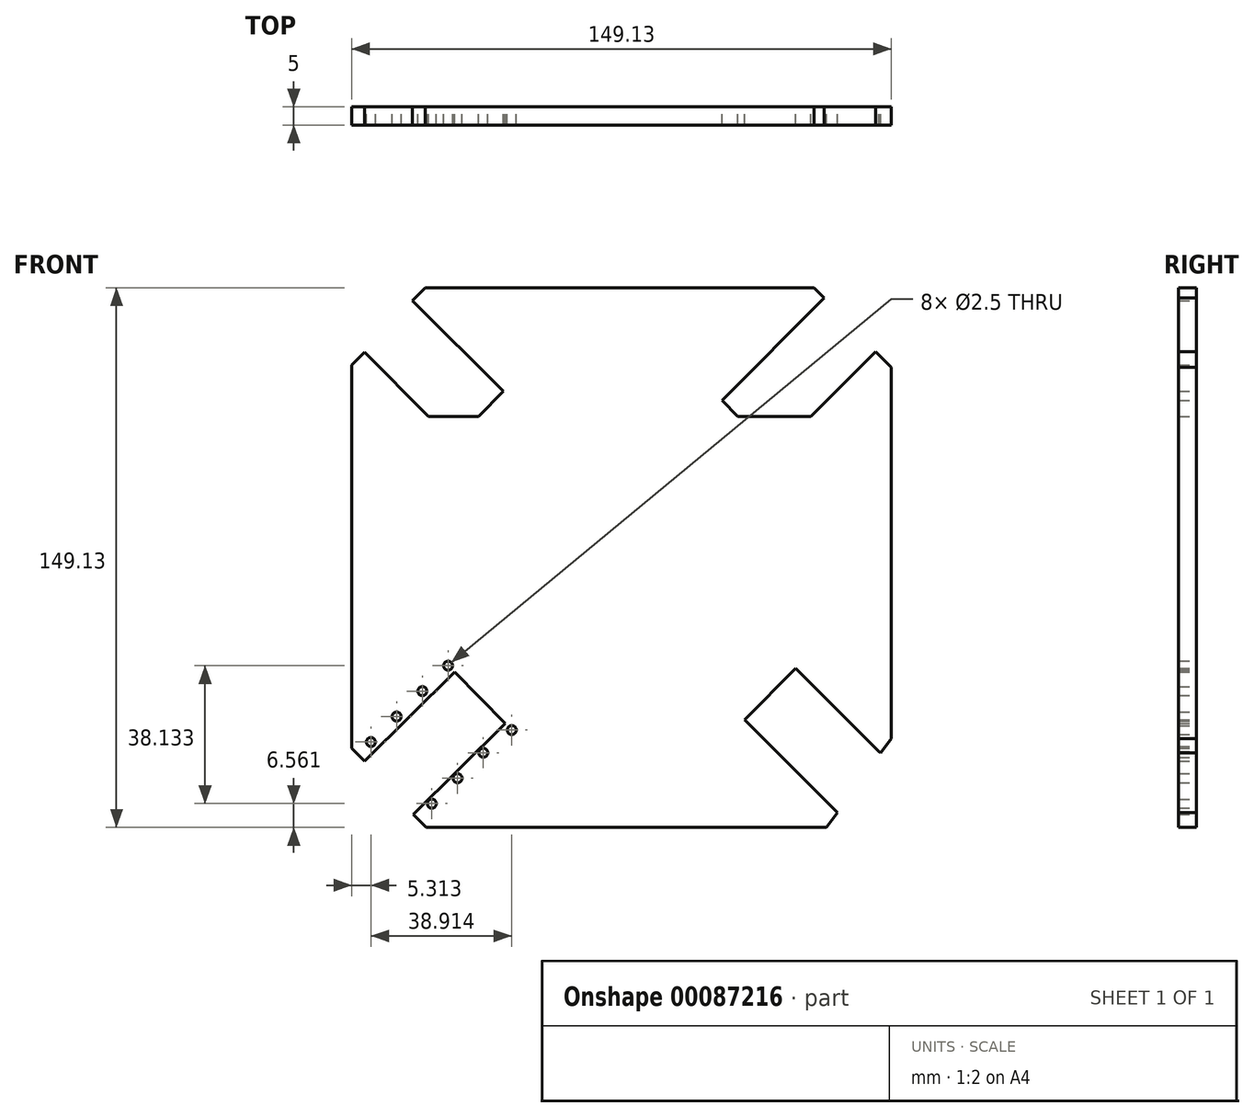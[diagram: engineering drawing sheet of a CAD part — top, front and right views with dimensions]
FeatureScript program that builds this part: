
annotation { "Feature Type Name" : "Feature", "Feature Type Description" : "" }
export const myFeature = defineFeature(function(context is Context, id is Id, definition is map)
    precondition{}
    {
        {
            var Q0;
            Q0=qCreatedBy(makeId("Front.planeOp"),FACE);
            var sketch = newSketch(context, id + "F0", { "sketchPlane" : qUnion([Q0])});
            skLineSegment(sketch, "E0.bottom", {"start": v(-47.44, 71.4) * mm, "end": v(60, 71.4) * mm});
            skLineSegment(sketch, "E0.top", {"start": v(-47.23, -77.73) * mm, "end": v(63.46, -77.73) * mm});
            skLineSegment(sketch, "E0.left", {"start": v(-67.78, 50.05) * mm, "end": v(-67.78, -55.88) * mm});
            skLineSegment(sketch, "E0.right", {"start": v(81.35, 49.41) * mm, "end": v(81.35, -3.16) * mm});
            skLineSegment(sketch, "E1", {"start": v(81.35, 71.4) * mm, "end": v(42.4, 32.45) * mm});
            skLineSegment(sketch, "E2", {"start": v(6.79, 34.12) * mm, "end": v(6.79, 71.4) * mm});
            skLineSegment(sketch, "E3.0", {"start": v(-64.24, 53.59) * mm, "end": v(-39.65, 29) * mm});
            skLineSegment(sketch, "E4.0", {"start": v(-50.97, 67.86) * mm, "end": v(-25.88, 42.77) * mm});
            skPoint(sketch, "E5.orphan", {"position": v(-30.5, -3.16) * mm});
            skPoint(sketch, "E6.orphan", {"position": v(-30.5, 34.12) * mm});
            skPoint(sketch, "E7.end.orphan", {"position": v(-30.5, 71.4) * mm});
            skPoint(sketch, "E8.orphan", {"position": v(-67.78, 71.4) * mm});
            skLineSegment(sketch, "E9.trimOffspring", {"start": v(54.92, -33.83) * mm, "end": v(77.9, -56.8) * mm});
            skLineSegment(sketch, "E10.trimOffspring", {"start": v(40.77, -47.97) * mm, "end": v(66.44, -73.64) * mm});
            skPoint(sketch, "E11.trimOffspring.end.orphan", {"position": v(81.35, -77.73) * mm});
            skLineSegment(sketch, "E12.0", {"start": v(-47.44, 71.4) * mm, "end": v(-27.61, 51.58) * mm});
            skLineSegment(sketch, "E13.0", {"start": v(-67.78, 50.05) * mm, "end": v(-44.42, 26.7) * mm});
            skLineSegment(sketch, "E14.0", {"start": v(-66, 51.82) * mm, "end": v(-44.42, 30.23) * mm});
            skLineSegment(sketch, "E15.0", {"start": v(-49.2, 69.63) * mm, "end": v(-29.38, 49.8) * mm});
            skLineSegment(sketch, "E16", {"start": v(-32.76, 35.88) * mm, "end": v(-59.78, 62.9) * mm});
            skLineSegment(sketch, "E17.0", {"start": v(62.84, 68.57) * mm, "end": v(34.56, 40.28) * mm});
            skLineSegment(sketch, "E18.0", {"start": v(77.01, 53.75) * mm, "end": v(49.05, 25.79) * mm});
            skLineSegment(sketch, "E19.0", {"start": v(60, 71.4) * mm, "end": v(31.73, 43.12) * mm});
            skLineSegment(sketch, "E20.0", {"start": v(81.35, 49.41) * mm, "end": v(53.39, 21.45) * mm});
            skLineSegment(sketch, "E21", {"start": v(31.73, 43.12) * mm, "end": v(53.39, 21.45) * mm});
            skPoint(sketch, "E22.orphan", {"position": v(6.79, 34.12) * mm});
            skPoint(sketch, "E23.orphan", {"position": v(44.07, -3.16) * mm});
            skLineSegment(sketch, "E24.0", {"start": v(28.05, 39.72) * mm, "end": v(49.26, 18.5) * mm});
            skLineSegment(sketch, "E25", {"start": v(54.92, -33.83) * mm, "end": v(40.77, -47.97) * mm});
            skLineSegment(sketch, "E26.0", {"start": v(37.24, -47.97) * mm, "end": v(64.95, -75.68) * mm});
            skLineSegment(sketch, "E27.0", {"start": v(30.17, -44.43) * mm, "end": v(63.46, -77.73) * mm});
            skLineSegment(sketch, "E28", {"start": v(54.83, -30.2) * mm, "end": v(79.67, -55.04) * mm});
            skLineSegment(sketch, "E29", {"start": v(54.83, -30.2) * mm, "end": v(37.24, -47.97) * mm});
            skLineSegment(sketch, "E30", {"start": v(51.38, -23.22) * mm, "end": v(81.35, -53.19) * mm});
            skPoint(sketch, "E31", {"position": v(68.1, -43.47) * mm});
            skLineSegment(sketch, "E32", {"start": v(46.04, -39.09) * mm, "end": v(74.17, -67.23) * mm});
            skPoint(sketch, "E33.0.start.orphan", {"position": v(-40.88, 30.23) * mm});
            skLineSegment(sketch, "E34", {"start": v(-39.65, 29) * mm, "end": v(-25.88, 42.77) * mm});
            skPoint(sketch, "E35.orphan", {"position": v(6.79, -40.45) * mm});
            skLineSegment(sketch, "E36.trimOffspring", {"start": v(-36.5, -32) * mm, "end": v(-64.26, -59.44) * mm});
            skLineSegment(sketch, "E37.trimOffspring", {"start": v(-25.32, -49.05) * mm, "end": v(-50.74, -74.17) * mm});
            skLineSegment(sketch, "E38", {"start": v(-40.03, -27.05) * mm, "end": v(-38.3, -28.8) * mm});
            skLineSegment(sketch, "E39", {"start": v(81.35, -3.16) * mm, "end": v(81.35, -53.19) * mm});
            skLineSegment(sketch, "E40", {"start": v(81.35, 49.41) * mm, "end": v(77.01, 53.75) * mm});
            skLineSegment(sketch, "E41", {"start": v(60, 71.4) * mm, "end": v(62.84, 68.57) * mm});
            skLineSegment(sketch, "E42", {"start": v(-67.78, 50.05) * mm, "end": v(-64.24, 53.59) * mm});
            skLineSegment(sketch, "E43", {"start": v(-47.44, 71.4) * mm, "end": v(-50.97, 67.86) * mm});
            skLineSegment(sketch, "E44", {"start": v(-67.78, -55.88) * mm, "end": v(-64.26, -59.44) * mm});
            skLineSegment(sketch, "E45", {"start": v(-47.23, -77.73) * mm, "end": v(-50.74, -74.17) * mm});
            skPoint(sketch, "E46.orphan", {"position": v(6.79, -3.16) * mm});
            skPoint(sketch, "E47.trimOffspring.end.orphan", {"position": v(81.35, -56.72) * mm});
            skLineSegment(sketch, "E48", {"start": v(63.46, -77.73) * mm, "end": v(66.44, -73.64) * mm});
            skLineSegment(sketch, "E49", {"start": v(77.9, -56.8) * mm, "end": v(78.43, -57.2) * mm});
            skLineSegment(sketch, "E50", {"start": v(79.67, -55.04) * mm, "end": v(79.88, -55.2) * mm});
            skPoint(sketch, "E51.start.orphan", {"position": v(67, -77.73) * mm});
            skLineSegment(sketch, "E52.trimOffspring", {"start": v(78.43, -57.2) * mm, "end": v(81.35, -53.19) * mm});
            skPoint(sketch, "E53.end.orphan", {"position": v(-67.78, -3.16) * mm});
            skPoint(sketch, "E54.end.orphan", {"position": v(6.79, -77.73) * mm});
            skLineSegment(sketch, "E55.trimOffspring", {"start": v(53.06, -60.26) * mm, "end": v(52.12, -62.85) * mm});
            skLineSegment(sketch, "E56", {"start": v(61.43, 69.98) * mm, "end": v(33.14, 41.7) * mm});
            skPoint(sketch, "E57", {"position": v(59.3, 65.03) * mm});
            skPoint(sketch, "E58", {"position": v(52.23, 57.96) * mm});
            skPoint(sketch, "E59", {"position": v(45.16, 50.9) * mm});
            skPoint(sketch, "E60", {"position": v(38.1, 43.82) * mm});
            skPoint(sketch, "E61", {"position": v(-62.47, -54.14) * mm});
            skPoint(sketch, "E62", {"position": v(-55.36, -47.1) * mm});
            skPoint(sketch, "E63", {"position": v(-48.25, -40.07) * mm});
            skPoint(sketch, "E64", {"position": v(-41.15, -33.04) * mm});
            skPoint(sketch, "E65", {"position": v(-38.33, -30.25) * mm});
            skLineSegment(sketch, "E66", {"start": v(-62.47, -54.14) * mm, "end": v(-62.46, -54.14) * mm});
            skLineSegment(sketch, "E67", {"start": v(-55.36, -47.1) * mm, "end": v(-55.35, -47.11) * mm});
            skLineSegment(sketch, "E68", {"start": v(-48.25, -40.07) * mm, "end": v(-48.24, -40.09) * mm});
            skCircle(sketch, "E69", {"center": v(-62.47, -54.14) * mm, "radius": 1.25 * mm});
            skCircle(sketch, "E70", {"center": v(-55.36, -47.1) * mm, "radius": 1.25 * mm});
            skCircle(sketch, "E71", {"center": v(-48.25, -40.07) * mm, "radius": 1.25 * mm});
            skCircle(sketch, "E72", {"center": v(-41.15, -33.04) * mm, "radius": 1.25 * mm});
            skCircle(sketch, "E73", {"center": v(-23.55, -50.84) * mm, "radius": 1.25 * mm});
            skCircle(sketch, "E74", {"center": v(-31.41, -57.11) * mm, "radius": 1.25 * mm});
            skCircle(sketch, "E75", {"center": v(-38.53, -64.14) * mm, "radius": 1.25 * mm});
            skCircle(sketch, "E76", {"center": v(-45.64, -71.17) * mm, "radius": 1.25 * mm});
            skPoint(sketch, "E77.end.orphan", {"position": v(-17.76, -47.09) * mm});
            skPoint(sketch, "E78.trimOffspring.end.orphan", {"position": v(-67.78, -77.73) * mm});
            skPoint(sketch, "E79.orphan", {"position": v(-21.27, -47.09) * mm});
            skPoint(sketch, "E80.orphan", {"position": v(-66.02, -57.66) * mm});
            skLineSegment(sketch, "E81.trimOffspring", {"start": v(-61.59, -55.03) * mm, "end": v(-60.7, -55.92) * mm});
            skLineSegment(sketch, "E82.trimOffspring", {"start": v(-54.48, -48) * mm, "end": v(-53.6, -48.9) * mm});
            skLineSegment(sketch, "E83.trimOffspring", {"start": v(-47.37, -40.96) * mm, "end": v(-46.48, -41.86) * mm});
            skLineSegment(sketch, "E84.trimOffspring", {"start": v(-39.37, -34.83) * mm, "end": v(-25.32, -49.05) * mm});
            skLineSegment(sketch, "E85", {"start": v(-32.76, 35.88) * mm, "end": v(-67.78, 35.88) * mm});
            skLineSegment(sketch, "E86", {"start": v(-32.76, 35.88) * mm, "end": v(81.35, 35.88) * mm});
            skSolve(sketch);
        }
        {
            var Q0;
            Q0 = qSketchRegion(id + "F0", true);
            extrude(context, id + "F1", {"entities" : qUnion([Q0]), "depth" : 5 * mm});
        }
    });
